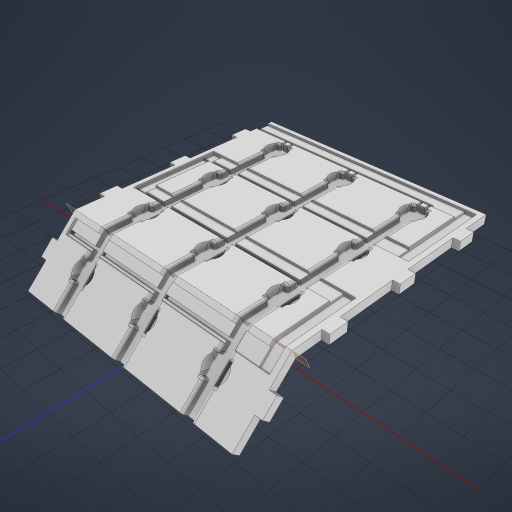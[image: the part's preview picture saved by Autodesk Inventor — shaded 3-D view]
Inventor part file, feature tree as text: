
AUTODESK INVENTOR PART (.ipt)
format: ipt  version: 2023 (Build 270158030, 158C)  size: 1,785,344 bytes
history: native  units: mm
features: extrude x17, sketch x17, delete_face x15, fillet x3, chamfer x3, pattern_linear x3, plane x3, mirror x1, split x1, direct_edit x1, boolean_combine x1, revolve x1
ambient origin geometry x8: Origin, YZ Plane, XZ Plane, XY Plane, X Axis, Y Axis, Z Axis, Center Point
bodies: Solid1 (feature_tree), Solid2 (feature_tree), Solid3 (feature_tree)
feature tree (66):
  extrude  "Extrusion1"  Depth=12.1mm
  extrude  "Extrusion2"  Depth=50.0mm
  extrude  "Extrusion3"  Depth=6.2mm
  fillet  "Fillet1"  Radius=3.8mm
  fillet  "Fillet2"  Radius=4.5mm
  extrude  "Extrusion5"  Depth=1.75mm
  chamfer  "Chamfer1"  Distance=4.5mm
  chamfer  "Chamfer2"  Distance=1.25mm
  extrude  "Extrusion6"  Depth=10.1mm
  delete_face  "Delete Face1"
  pattern_linear  "Rectangular Pattern1"  Count1=3  [1 undecoded]
  extrude  "Extrusion8"  Depth=7.0mm
  extrude  "Extrusion10"  Depth=10.1mm
  extrude  "Extrusion11"  Depth=10.0mm
  extrude  "Extrusion12"  Depth=4.5mm
  extrude  "Extrusion13"  Depth=10.0mm
  fillet  "Fillet3"  Radius=10.0mm
  extrude  "Extrusion14"  Depth=2.0mm
  extrude  "Extrusion15"  Depth=10.0mm
  pattern_linear  "Rectangular Pattern5"  Spacing1=4.5mm  [1 undecoded]
  pattern_linear  "Rectangular Pattern6"  Spacing1=2.0mm  [1 undecoded]
  delete_face  "Delete Face2"
  extrude  "Extrusion16"  Depth=10.0mm TaperAngle=0.0deg
  chamfer  "Chamfer3"  Distance=50.0mm
  delete_face  "Delete Face3"
  delete_face  "Delete Face4"
  extrude  "Extrusion17"  Depth=50.0mm
  extrude  "Extrusion18"  Depth=10.0mm
  extrude  "Extrusion19"  Depth=10.0mm TaperAngle=0.0deg
  plane  "Work Plane1"
  extrude  "Extrusion20"  Depth=10.0mm
  plane  "Work Plane2"
  mirror  "Mirror1"
  split  "Split1"
  direct_edit  "Direct Edit1"
  boolean_combine  "Combine1"
  delete_face  "Delete Face5"
  delete_face  "Delete Face6"
  delete_face  "Delete Face7"
  delete_face  "Delete Face8"
  delete_face  "Delete Face9"
  delete_face  "Delete Face10"
  delete_face  "Delete Face11"
  delete_face  "Delete Face12"
  delete_face  "Delete Face13"
  delete_face  "Delete Face14"
  delete_face  "Delete Face15"
  plane  "Work Plane3"
  sketch  "Sketch1"  dims[d0=12.1mm d1=12.1mm]
  sketch  "Sketch2"  dims[d2=50.0mm d3=50.0mm]
  sketch  "Sketch3"  dims[d4=4.5mm d5=0.0mm d6=6.2mm d7=3.8mm d8=4.5mm d9=0.0mm]
  sketch  "Sketch5"  dims[d10=1.5mm d11=0.0mm d15=1.75mm]
  sketch  "Sketch6"  dims[d16=1.75mm]
  sketch  "Sketch8"  dims[d17=13.0mm d18=4.5mm d19=0.0mm d20=1.25mm d21=2.0mm d22=12.997467mm]
  sketch  "Sketch10"  dims[d23=1.25mm d24=2.0mm d25=12.997467mm d26=10.1mm]
  sketch  "Sketch11"  dims[d27=1.5mm d28=0.0mm d29=30.0mm d31=50.0mm d32=40.0mm d34=50.0mm]
  sketch  "Sketch12"  dims[d39=7.0mm d40=7.0mm]
  sketch  "Sketch13"  dims[d41=1.5mm d42=0.0mm d46=10.1mm]
  sketch  "Sketch14"  dims[d47=10.0mm d48=0.0mm d49=3.55mm]
  sketch  "Sketch15"  dims[d50=4.5mm d51=0.0mm d52=1.2mm]
  sketch  "Sketch16"  dims[d53=5.0mm d54=5.0mm d55=10.0mm d56=0.0mm]
  sketch  "Sketch17"  dims[d60=130.0mm d61=2.0mm]
  sketch  "Sketch18"  dims[d62=10.0mm d63=0.0mm d64=1.25mm]
  sketch  "Sketch19"  dims[d69=3.55mm]
  sketch  "Sketch20"  dims[d70=3.55mm d71=4.5mm d72=0.0mm d73=2.0mm d74=8.0mm d75=0.0mm d82=30.0mm d84=50.0mm d85=40.0mm d87=50.0mm d88=1.5mm d89=8.0mm d90=0.0mm d91=1.0mm d92=2.0mm d93=12.997467mm d94=7.0mm d95=7.0mm d96=7.0mm d97=1.25mm d98=0.0mm d100=12.0mm d101=6.0mm d102=40.0mm d104=50.0mm d105=10.0mm d107=10.0mm d109=4.5mm d110=0.0mm d111=2.0mm d112=2.0mm d113=4.0mm d114=0.0mm d115=2.0mm d116=160.0mm d117=30.0mm d119=50.0mm d120=10.0mm d122=10.0mm d124=3.25mm d125=0.0mm d126=-50.0mm d127=45.0deg]
  revolve  "Rotate1"  [1 undecoded]
note: 4 required parameter values undecoded (feature->parameter linkage not recoverable at this tier; creation-order binding heuristic only, values carry confidence <= 0.55)